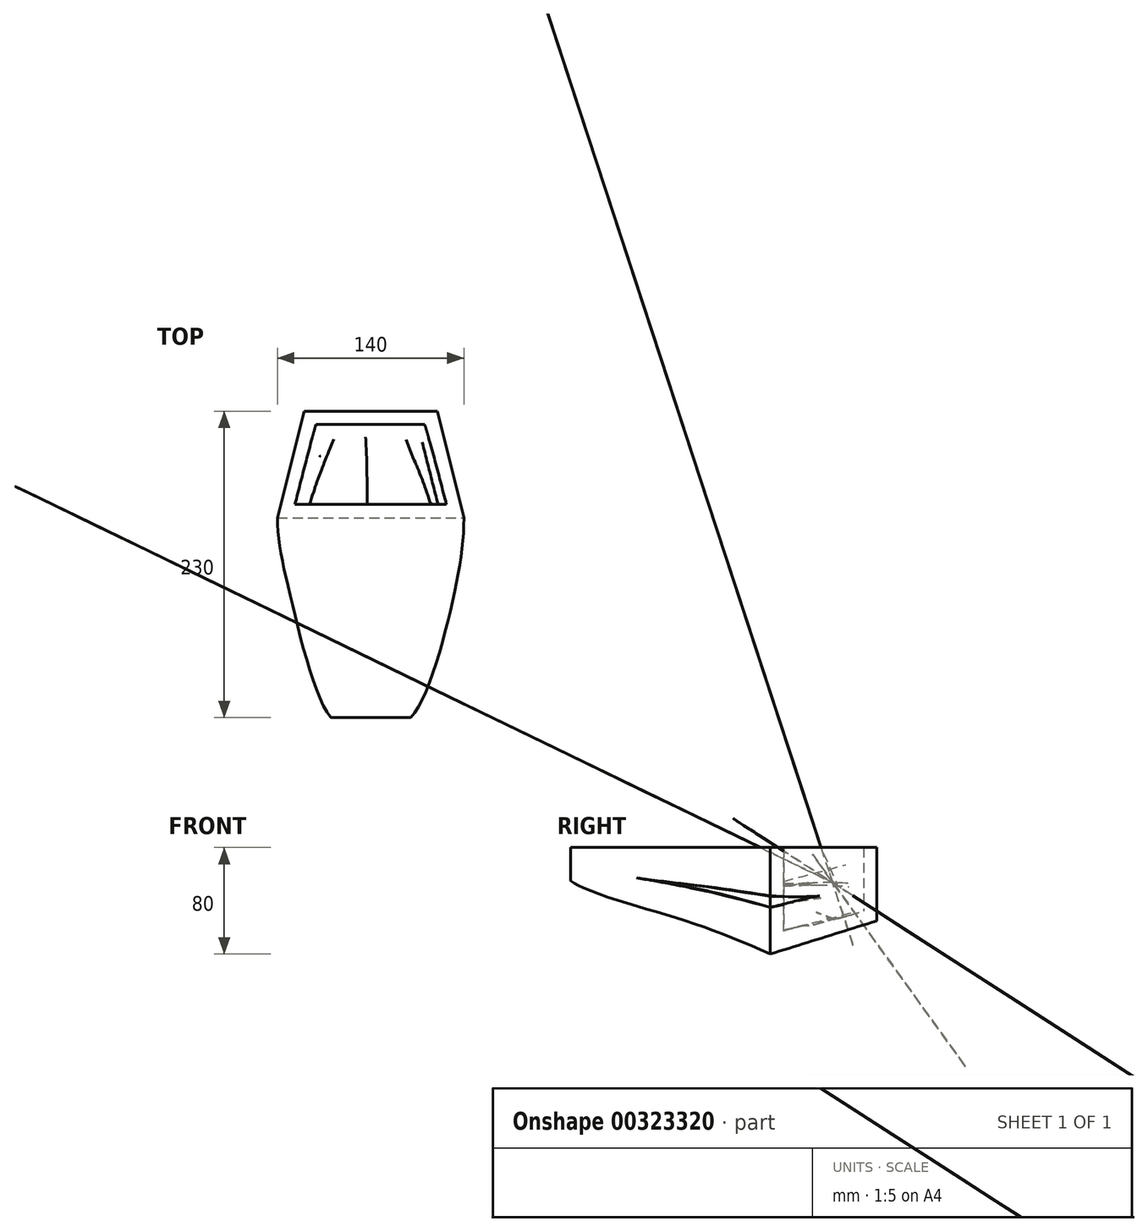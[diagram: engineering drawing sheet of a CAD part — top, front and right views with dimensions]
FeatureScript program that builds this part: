
annotation { "Feature Type Name" : "Feature", "Feature Type Description" : "" }
export const myFeature = defineFeature(function(context is Context, id is Id, definition is map)
    precondition{}
    {
        {
            var Q0;
            Q0=qCreatedBy(makeId("Front.planeOp"),FACE);
            var sketch = newSketch(context, id + "F0", { "sketchPlane" : qUnion([Q0])});
            skFitSpline(sketch, "E0", {"points": [v(-70, 0) * mm, v(-55, -45) * mm, v(-35, -36.68) * mm, v(0, -80) * mm, v(35, -37.16) * mm, v(55, -45) * mm, v(70, 0) * mm], "startDerivative": vector(82.68, -359.78) * mm, "endDerivative": vector(82.68, 348.04) * mm});
            skLineSegment(sketch, "E1", {"start": v(-70, 0) * mm, "end": v(70, 0) * mm});
            skSolve(sketch);
        }
        {
            var Q0;
            Q0=qCreatedBy(makeId("Front.planeOp"),FACE);
            cPlane(context, id + "F1", {"entities" : qUnion([Q0]), "cplaneType" : CPlaneType.OFFSET, "offset" : 80 * mm, "oppositeDirection" : true, "width" : 150 * mm, "height" : 150 * mm});
        }
        {
            var Q0;
            Q0=qCreatedBy(id+"F1.planeOp",FACE);
            var sketch = newSketch(context, id + "F2", { "sketchPlane" : qUnion([Q0])});
            skFitSpline(sketch, "E2", {"points": [v(-50, 0) * mm, v(-28, -39.82) * mm, v(0, -55) * mm, v(28, -34.27) * mm, v(50, 0) * mm], "startDerivative": vector(87.8, -154.23) * mm, "endDerivative": vector(92.8, 123.15) * mm});
            skLineSegment(sketch, "E3", {"start": v(-50, 0) * mm, "end": v(50, 0) * mm});
            skSolve(sketch);
        }
        {
            var Q0;
            Q0=qCreatedBy(makeId("Top.planeOp"),FACE);
            var sketch = newSketch(context, id + "F3", { "sketchPlane" : qUnion([Q0])});
            skFitSpline(sketch, "E4", {"points": [v(70, 0) * mm, v(67, 34) * mm, v(60, 58.44) * mm, v(50, 80) * mm], "startDerivative": vector(0, 62.9) * mm, "endDerivative": vector(-48.5, 70.18) * mm});
            skFitSpline(sketch, "E5", {"points": [v(-50, 80) * mm, v(-60, 53.76) * mm, v(-70, 0) * mm], "startDerivative": vector(-35.93, -36.56) * mm, "endDerivative": vector(-15.45, -118.58) * mm});
            skSolve(sketch);
        }
        {
            var Q0;
            Q0 = qSketchRegion(id + "F0", true);
            var Q1;
            Q1 = qSketchRegion(id + "F2", true);
            var Q2;
            Q2 = qConstructionFilter(qBodyType(qCreatedBy(id + "F3" ,EDGE), BodyType.WIRE), ConstructionObject.NO);
            loft(context, id + "F4", {"sheetProfilesArray" : [{ "sheetProfileEntities" : qUnion([Q0]) }, { "sheetProfileEntities" : qUnion([Q1]) }], "guidesArray" : [{ "guideEntities" : qUnion([Q2]), "guideDerivativeType" : LoftGuideDerivativeType.DEFAULT, "guideDerivativeMagnitude" : 1 }]});
        }
        {
            var Q0;
            {var subQ0=sQuery(id+"F2.wireOp",EDGE,"E3");var subQ1=sQuery(id+"F2.wireOp",EDGE,"E2");var subQ2=sQuery(id+"F0.wireOp",EDGE,"E1");var subQ3=sQuery(id+"F0.wireOp",EDGE,"E0");Q0=makeQuery(id+"F4.opLoft","SWEPT_FACE",FACE,{"disambiguationData":[OSD([subQ3,subQ2,subQ1,subQ0]),TDD([makeQuery(id+"F0.imprint","INTERSECT",VERTEX,{"disambiguationData":[OD(0.0)],"derivedFrom":[subQ3,subQ2]}),makeQuery(id+"F0.imprint","INTERSECT",VERTEX,{"disambiguationData":[OD(1.0)],"derivedFrom":[subQ3,subQ2]}),makeQuery(id+"F0.imprint","IMPRINT",EDGE,{"derivedFrom":subQ2}),makeQuery(id+"F2.imprint","INTERSECT",VERTEX,{"disambiguationData":[OD(0.0)],"derivedFrom":[subQ1,subQ0]}),makeQuery(id+"F2.imprint","INTERSECT",VERTEX,{"disambiguationData":[OD(1.0)],"derivedFrom":[subQ1,subQ0]}),makeQuery(id+"F2.imprint","IMPRINT",EDGE,{"derivedFrom":subQ0})])]});}
            shell(context, id + "F5", {"entities" : qUnion([Q0]), "thickness" : 10 * mm});
        }
        {
            var Q0;
            Q0=qCreatedBy(makeId("Front.planeOp"),FACE);
            cPlane(context, id + "F6", {"entities" : qUnion([Q0]), "cplaneType" : CPlaneType.OFFSET, "offset" : 150 * mm, "width" : 150 * mm, "height" : 150 * mm});
        }
        {
            var Q0;
            Q0=qCreatedBy(id+"F6.planeOp",FACE);
            var sketch = newSketch(context, id + "F7", { "sketchPlane" : qUnion([Q0])});
            skFitSpline(sketch, "E6", {"points": [v(-30, 0) * mm, v(-21, -13.28) * mm, v(0, -25) * mm, v(21, -11.94) * mm, v(30, 0) * mm], "startDerivative": vector(26.59, -58.35) * mm, "endDerivative": vector(27.54, 50.48) * mm});
            skLineSegment(sketch, "E7", {"start": v(-30, 0) * mm, "end": v(30, 0) * mm});
            skSolve(sketch);
        }
        {
            var Q0;
            Q0=qCreatedBy(makeId("Top.planeOp"),FACE);
            var sketch = newSketch(context, id + "F8", { "sketchPlane" : qUnion([Q0])});
            skFitSpline(sketch, "E8", {"points": [v(70, 0) * mm, v(60, -69.23) * mm, v(30, -150) * mm], "startDerivative": vector(0, -130.52) * mm, "endDerivative": vector(-68.44, -70.99) * mm});
            skFitSpline(sketch, "E9", {"points": [v(-70, 0) * mm, v(-60, -59.99) * mm, v(-30, -150) * mm], "startDerivative": vector(0, -119.35) * mm, "endDerivative": vector(64.82, -82.09) * mm});
            skSolve(sketch);
        }
        {
            var Q1;
            Q1=makeQuery(id+"F0.imprint","IMPRINT",FACE,{"disambiguationData":[TD([[makeQuery(id+"F0.imprint","IMPRINT",EDGE,{"derivedFrom":sQuery(id+"F0.wireOp",EDGE,"E0")}),1.0]])]});
            var Q2;
            Q2=makeQuery(id+"F7.imprint","IMPRINT",FACE,{"disambiguationData":[TD([[makeQuery(id+"F7.imprint","IMPRINT",EDGE,{"derivedFrom":sQuery(id+"F7.wireOp",EDGE,"E6")}),1.0]])]});
            var Q3;
            Q3=sQuery(id+"F8.wireOp",EDGE,"E8");
            var Q4;
            Q4=sQuery(id+"F8.wireOp",EDGE,"E9");
            loft(context, id + "F9", {"operationType" : NewBodyOperationType.ADD, "addGuides" : true, "sheetProfilesArray" : [{ "sheetProfileEntities" : qUnion([Q1]) }, { "sheetProfileEntities" : qUnion([Q2]) }], "guidesArray" : [{ "guideEntities" : qUnion([Q3]), "guideDerivativeType" : LoftGuideDerivativeType.DEFAULT, "guideDerivativeMagnitude" : 1 }, { "guideEntities" : qUnion([Q4]), "guideDerivativeType" : LoftGuideDerivativeType.DEFAULT, "guideDerivativeMagnitude" : 1 }]});
        }
    });
